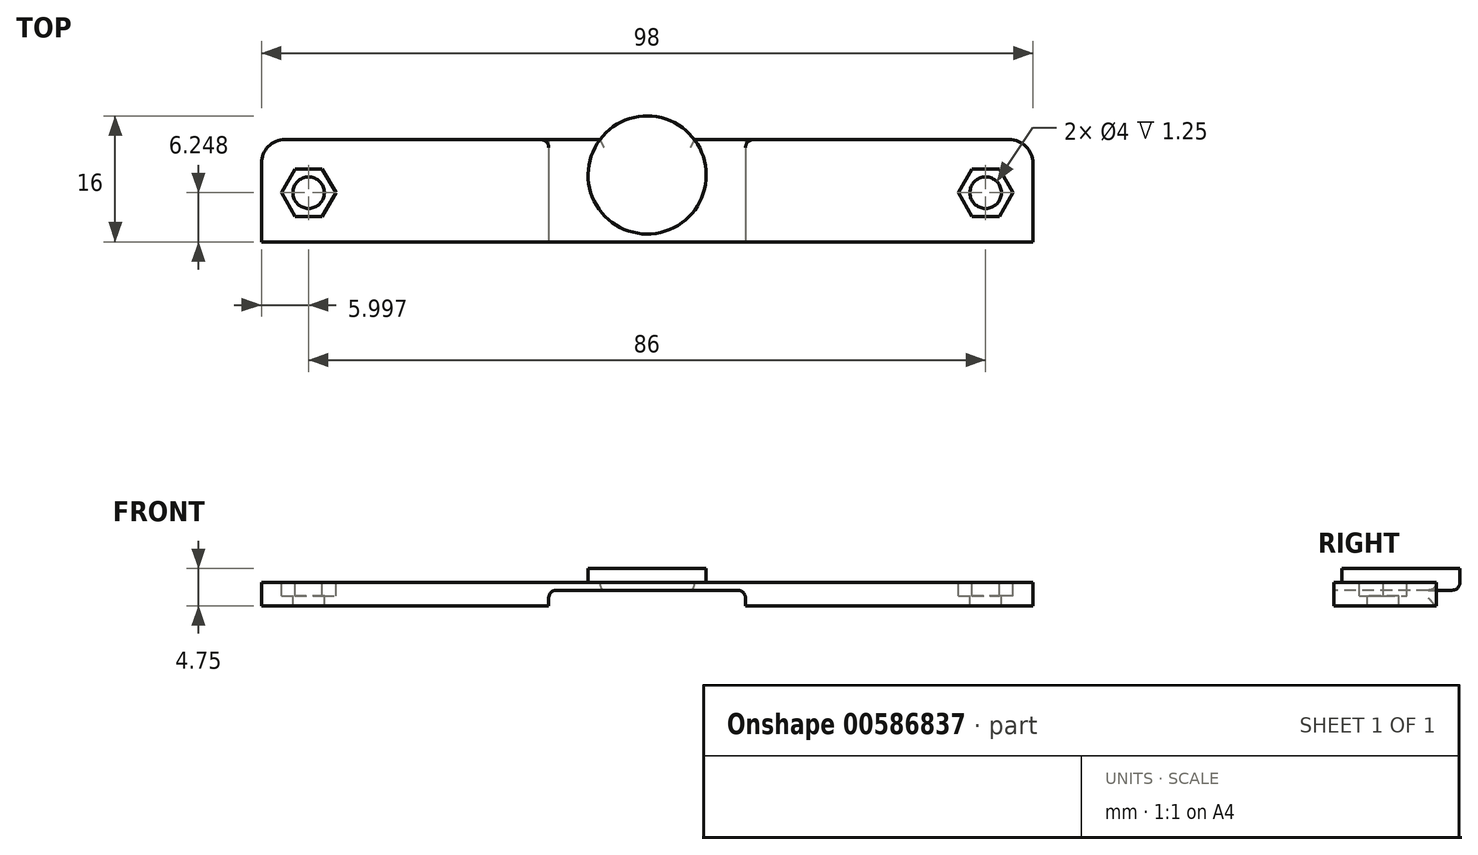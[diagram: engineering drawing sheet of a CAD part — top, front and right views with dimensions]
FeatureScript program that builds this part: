
annotation { "Feature Type Name" : "Feature", "Feature Type Description" : "" }
export const myFeature = defineFeature(function(context is Context, id is Id, definition is map)
    precondition{}
    {
        {
            var Q0;
            Q0=qCreatedBy(makeId("Top.planeOp"),FACE);
            var sketch = newSketch(context, id + "F0", { "sketchPlane" : qUnion([Q0])});
            skLineSegment(sketch, "E0.bottom", {"start": v(-43.24, -26.78) * mm, "end": v(54.76, -26.78) * mm});
            skLineSegment(sketch, "E0.top", {"start": v(-43.24, -13.78) * mm, "end": v(54.76, -13.78) * mm});
            skLineSegment(sketch, "E0.left", {"start": v(-43.24, -26.78) * mm, "end": v(-43.24, -13.78) * mm});
            skLineSegment(sketch, "E0.right", {"start": v(54.76, -26.78) * mm, "end": v(54.76, -13.78) * mm});
            skSolve(sketch);
        }
        {
            var Q0;
            Q0 = qSketchRegion(id + "F0", true);
            extrude(context, id + "F1", {"entities" : qUnion([Q0]), "depth" : 3 * mm, "offsetDistance" : 25 * mm});
        }
        {
            var Q0;
            Q0=makeQuery(id+"F1.opExtrude","SWEPT_EDGE",EDGE,{"disambiguationData":[OSD([sQuery(id+"F0.wireOp",EDGE,"E0.top"),sQuery(id+"F0.wireOp",EDGE,"E0.left")])]});
            var Q1;
            Q1=makeQuery(id+"F1.opExtrude","SWEPT_EDGE",EDGE,{"disambiguationData":[OSD([sQuery(id+"F0.wireOp",EDGE,"E0.top"),sQuery(id+"F0.wireOp",EDGE,"E0.right")])]});
            fillet(context, id + "F2", {"entities" : qUnion([Q0, Q1]), "radius" : 3 * mm, "tangentPropagation" : true, "allowEdgeOverflow" : false});
        }
        {
            var Q0;
            Q0=makeQuery(id+"F1.opExtrude","CAP_FACE",FACE,{"disambiguationData":[OSD([sQuery(id+"F0.wireOp",EDGE,"E0.bottom"),sQuery(id+"F0.wireOp",EDGE,"E0.top"),sQuery(id+"F0.wireOp",EDGE,"E0.left"),sQuery(id+"F0.wireOp",EDGE,"E0.right")])],"isStart":false});
            var sketch = newSketch(context, id + "F3", { "sketchPlane" : qUnion([Q0])});
            skCircle(sketch, "E1", {"center": v(48.76, -20.53) * mm, "radius": 2 * mm});
            skCircle(sketch, "E2", {"center": v(-37.24, -20.53) * mm, "radius": 2 * mm});
            skSolve(sketch);
        }
        {
            var Q0;
            Q0=qSketchRegion(id+"F3",true);
            extrude(context, id + "F4", {"entities" : qUnion([Q0]), "operationType" : NewBodyOperationType.REMOVE, "oppositeDirection" : true, "depth" : 20 * mm, "offsetDistance" : 25 * mm});
        }
        {
            var Q0;
            Q0=qCreatedBy(makeId("Top.planeOp"),FACE);
            var sketch = newSketch(context, id + "F5", { "sketchPlane" : qUnion([Q0])});
            skCircle(sketch, "E3", {"center": v(5.76, -18.28) * mm, "radius": 7.5 * mm});
            skSolve(sketch);
        }
        {
            var Q0;
            Q0=makeQuery(id+"F5.imprint","IMPRINT",FACE,{"disambiguationData":[TD([[makeQuery(id+"F5.imprint","IMPRINT",EDGE,{"derivedFrom":sQuery(id+"F5.wireOp",EDGE,"E3")}),1.0]])]});
            extrude(context, id + "F6", {"entities" : qUnion([Q0]), "operationType" : NewBodyOperationType.ADD, "depth" : 4.75 * mm, "offsetDistance" : 25 * mm});
        }
        {
            var Q0;
            Q0=makeQuery(id+"F1.opExtrude","CAP_FACE",FACE,{"disambiguationData":[OSD([sQuery(id+"F0.wireOp",EDGE,"E0.bottom"),sQuery(id+"F0.wireOp",EDGE,"E0.top"),sQuery(id+"F0.wireOp",EDGE,"E0.left"),sQuery(id+"F0.wireOp",EDGE,"E0.right")])],"isStart":false});
            var sketch = newSketch(context, id + "F7", { "sketchPlane" : qUnion([Q0])});
            skCircle(sketch, "E4.cCircle", {"center": v(-37.24, -20.53) * mm, "radius": 3.46 * mm, "construction": true});
            skLineSegment(sketch, "E4.0", {"start": v(-35.51, -17.53) * mm, "end": v(-33.78, -20.53) * mm});
            skLineSegment(sketch, "E4.1", {"start": v(-33.78, -20.53) * mm, "end": v(-35.51, -23.53) * mm});
            skLineSegment(sketch, "E4.2", {"start": v(-35.51, -23.53) * mm, "end": v(-38.98, -23.53) * mm});
            skLineSegment(sketch, "E4.3", {"start": v(-38.98, -23.53) * mm, "end": v(-40.7, -20.53) * mm});
            skLineSegment(sketch, "E4.4", {"start": v(-40.7, -20.53) * mm, "end": v(-38.98, -17.53) * mm});
            skLineSegment(sketch, "E4.5", {"start": v(-38.98, -17.53) * mm, "end": v(-35.51, -17.53) * mm});
            skCircle(sketch, "E5.cCircle", {"center": v(48.76, -20.53) * mm, "radius": 3.46 * mm, "construction": true});
            skLineSegment(sketch, "E5.0", {"start": v(47.02, -17.53) * mm, "end": v(50.49, -17.53) * mm});
            skLineSegment(sketch, "E5.1", {"start": v(50.49, -17.53) * mm, "end": v(52.22, -20.53) * mm});
            skLineSegment(sketch, "E5.2", {"start": v(52.22, -20.53) * mm, "end": v(50.49, -23.53) * mm});
            skLineSegment(sketch, "E5.3", {"start": v(50.49, -23.53) * mm, "end": v(47.02, -23.53) * mm});
            skLineSegment(sketch, "E5.4", {"start": v(47.02, -23.53) * mm, "end": v(45.3, -20.53) * mm});
            skLineSegment(sketch, "E5.5", {"start": v(45.3, -20.53) * mm, "end": v(47.02, -17.53) * mm});
            skSolve(sketch);
        }
        {
            var Q0;
            Q0 = qSketchRegion(id + "F7", true);
            extrude(context, id + "F8", {"entities" : qUnion([Q0]), "operationType" : NewBodyOperationType.REMOVE, "oppositeDirection" : true, "depth" : 1.75 * mm, "offsetDistance" : 25 * mm});
        }
        {
            var Q0;
            Q0=makeQuery(id+"F6.boolean.opBoolean","MERGE",FACE,{"derivedFrom":[makeQuery(id+"F1.opExtrude","CAP_FACE",FACE,{"disambiguationData":[OSD([sQuery(id+"F0.wireOp",EDGE,"E0.bottom"),sQuery(id+"F0.wireOp",EDGE,"E0.top"),sQuery(id+"F0.wireOp",EDGE,"E0.left"),sQuery(id+"F0.wireOp",EDGE,"E0.right")])],"isStart":true}),makeQuery(id+"F6.opExtrude","CAP_FACE",FACE,{"disambiguationData":[OSD([sQuery(id+"F5.wireOp",EDGE,"E3")])],"isStart":true})]});
            var sketch = newSketch(context, id + "F9", { "sketchPlane" : qUnion([Q0])});
            skLineSegment(sketch, "E6.bottom", {"start": v(-6.74, 10.78) * mm, "end": v(18.26, 10.78) * mm});
            skLineSegment(sketch, "E6.top", {"start": v(-6.74, 26.78) * mm, "end": v(18.26, 26.78) * mm});
            skLineSegment(sketch, "E6.left", {"start": v(-6.74, 10.78) * mm, "end": v(-6.74, 26.78) * mm});
            skLineSegment(sketch, "E6.right", {"start": v(18.26, 10.78) * mm, "end": v(18.26, 26.78) * mm});
            skSolve(sketch);
        }
        {
            var Q0;
            Q0 = qSketchRegion(id + "F9", true);
            extrude(context, id + "F10", {"entities" : qUnion([Q0]), "operationType" : NewBodyOperationType.REMOVE, "oppositeDirection" : true, "depth" : 2 * mm, "offsetDistance" : 25 * mm});
        }
        {
            var Q0;
            Q0=makeQuery(id+"F10.boolean.opBoolean","COPY",EDGE,{"derivedFrom":makeQuery(id+"F10.opExtrude","CAP_EDGE",EDGE,{"disambiguationData":[OSD([sQuery(id+"F9.wireOp",EDGE,"E6.right")])],"isStart":false})});
            var Q1;
            Q1=makeQuery(id+"F10.boolean.opBoolean","COPY",EDGE,{"derivedFrom":makeQuery(id+"F10.opExtrude","CAP_EDGE",EDGE,{"disambiguationData":[OSD([sQuery(id+"F9.wireOp",EDGE,"E6.left")])],"isStart":false})});
            var Q2;
            {var subQ0=sQuery(id+"F0.wireOp",EDGE,"E0.right");var subQ1=sQuery(id+"F0.wireOp",EDGE,"E0.top");Q2=makeQuery(id+"F10.boolean.opBoolean","INTERSECT",EDGE,{"derivedFrom":[makeQuery(id+"F6.boolean.opBoolean","SPLIT",FACE,{"disambiguationData":[TD([makeQuery(id+"F2.opFillet","BLEND_FACE",FACE,{"disambiguationData":[OSD([subQ1,subQ0])]})])],"derivedFrom":makeQuery(id+"F1.opExtrude","SWEPT_FACE",FACE,{"disambiguationData":[OSD([subQ1])]})}),makeQuery(id+"F10.opExtrude","CAP_FACE",FACE,{"disambiguationData":[OSD([sQuery(id+"F9.wireOp",EDGE,"E6.bottom"),sQuery(id+"F9.wireOp",EDGE,"E6.top"),sQuery(id+"F9.wireOp",EDGE,"E6.left"),sQuery(id+"F9.wireOp",EDGE,"E6.right")])],"isStart":false})]});}
            var Q3;
            Q3=makeQuery(id+"F10.boolean.opBoolean","INTERSECT",EDGE,{"derivedFrom":[makeQuery(id+"F6.opExtrude","SWEPT_FACE",FACE,{"disambiguationData":[OSD([sQuery(id+"F5.wireOp",EDGE,"E3")])]}),makeQuery(id+"F10.opExtrude","CAP_FACE",FACE,{"disambiguationData":[OSD([sQuery(id+"F9.wireOp",EDGE,"E6.bottom"),sQuery(id+"F9.wireOp",EDGE,"E6.top"),sQuery(id+"F9.wireOp",EDGE,"E6.left"),sQuery(id+"F9.wireOp",EDGE,"E6.right")])],"isStart":false})]});
            var Q4;
            {var subQ1=sQuery(id+"F0.wireOp",EDGE,"E0.left");var subQ2=sQuery(id+"F0.wireOp",EDGE,"E0.top");Q4=makeQuery(id+"F10.boolean.opBoolean","INTERSECT",EDGE,{"derivedFrom":[makeQuery(id+"F6.boolean.opBoolean","SPLIT",FACE,{"disambiguationData":[TD([makeQuery(id+"F2.opFillet","BLEND_FACE",FACE,{"disambiguationData":[OSD([subQ2,subQ1])]})])],"derivedFrom":makeQuery(id+"F1.opExtrude","SWEPT_FACE",FACE,{"disambiguationData":[OSD([subQ2])]})}),makeQuery(id+"F10.opExtrude","CAP_FACE",FACE,{"disambiguationData":[OSD([sQuery(id+"F9.wireOp",EDGE,"E6.bottom"),sQuery(id+"F9.wireOp",EDGE,"E6.top"),sQuery(id+"F9.wireOp",EDGE,"E6.left"),sQuery(id+"F9.wireOp",EDGE,"E6.right")])],"isStart":false})]});}
            var Q5;
            Q5=makeQuery(id+"F10.boolean.opBoolean","COPY",EDGE,{"derivedFrom":makeQuery(id+"F10.opExtrude","CAP_EDGE",EDGE,{"disambiguationData":[OSD([sQuery(id+"F9.wireOp",EDGE,"E6.top")])],"isStart":false})});
            fillet(context, id + "F11", {"entities" : qUnion([Q0, Q1, Q2, Q3, Q4, Q5]), "radius" : 1 * mm, "tangentPropagation" : true, "allowEdgeOverflow" : false});
        }
    });
